# Revit family: Toilet_Tank-In_Wall-KOHLER-INSTAFIT-K-20081IN_1
name_source: partatom
category: Plumbing Fixtures
revit_build: Autodesk Revit 2017 (Build: 20160225_1515(x64)
units: mm (PartAtom-declared; Revit-internal decimal feet)

## family parameters
Cut with Voids When Loaded = No
Host = Face
OmniClass Number = 23.31.19.00
OmniClass Title = Toilets
Part Type = Normal
Room Calculation Point = No
Round Connector Dimension = Use Diameter
Shared = No

## types (2) — shared parameters
ADA Compliant = No
Assembly Code = D2010100
CW Connection = Yes
Cold Water Inlet = Cold Water Inlet
Cold Water Outlet = Cold Water Outlet
Date Modified = 01/08/2021
Default Elevation = 0"
Finish = Kohler-Metal-NA-Stainless
Flow Rate = 0 GPM
Flush Rate- GPF = GPF
Flush Rate- LPF = LPF
HW Connection = No
Height = 41 1/4"
Hot Water Inlet = Hot Water Inlet
Length = 3 3/4"
Manufacturer = KOHLER Co.
Master Format 2014 = 22 42 13.13
Master Format 2014 Name = Residential Water Closets
Material = Carbon Steel Tube
Pressure = 0.00 psi
Product Name = INSTAFIT
Seat Included = No
URL = https://www.kohler.co.in
Vent Connection = No
Waste Connection = No
Waste Water Outlet = Waste Water Outlet
WaterSense Certified = No
Width = 22 1/16"

## per-type parameters (varying)
| type | Description | Model | Type |
| Mechanical Actuator,NA-Stainless | Mechanical W/ Connector ACC | K-20081IN-M-NA | 1 |
| Pneumatic Actuator,NA-Stainless | Pneumatic W/ Connector ACC | K-20081IN-P-NA | 2 |

## geometry (parser evidence)
native form markers: Sweep x4
no freeform markers — native parametric forms only
